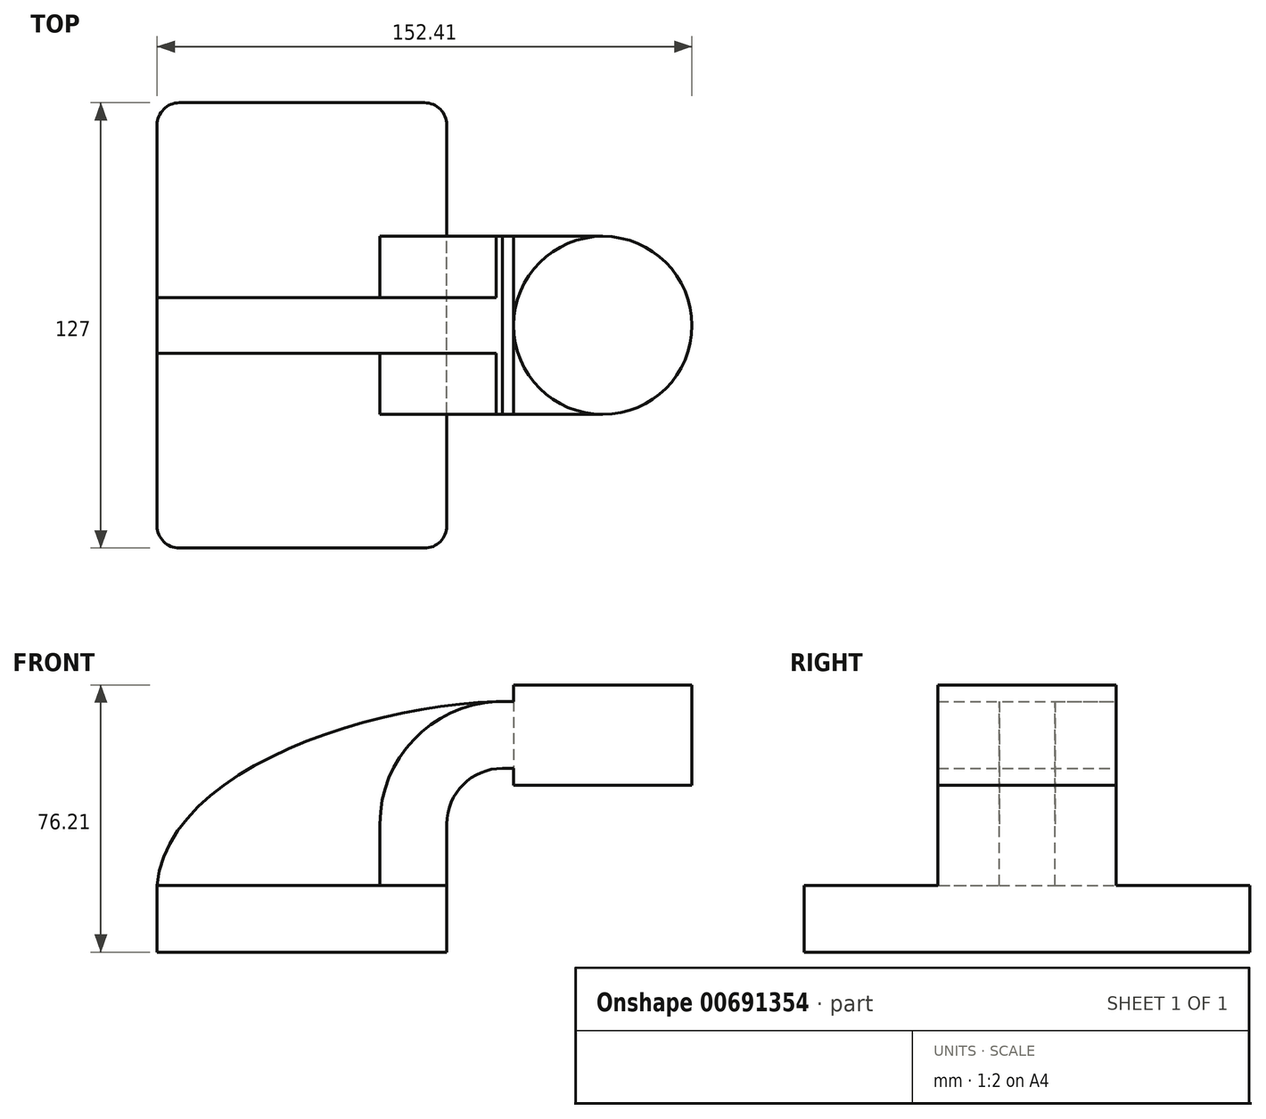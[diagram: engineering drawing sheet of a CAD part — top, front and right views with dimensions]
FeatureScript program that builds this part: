
annotation { "Feature Type Name" : "Feature", "Feature Type Description" : "" }
export const myFeature = defineFeature(function(context is Context, id is Id, definition is map)
    precondition{}
    {
        {
            var Q0;
            Q0=qCreatedBy(makeId("Front.planeOp"),FACE);
            var sketch = newSketch(context, id + "F0", { "sketchPlane" : qUnion([Q0])});
            skLineSegment(sketch, "E0.bottom", {"start": v(-41.28, 9.52) * mm, "end": v(41.27, 9.53) * mm});
            skLineSegment(sketch, "E0.top", {"start": v(-41.28, -9.52) * mm, "end": v(41.28, -9.52) * mm});
            skLineSegment(sketch, "E0.left", {"start": v(-41.28, 9.52) * mm, "end": v(-41.28, -9.53) * mm});
            skLineSegment(sketch, "E0.right", {"start": v(41.27, 9.53) * mm, "end": v(41.28, -9.52) * mm});
            skPoint(sketch, "E0.middle", {"position": v(0, 0) * mm});
            skLineSegment(sketch, "E1.bottom", {"start": v(60.32, 38.1) * mm, "end": v(111.12, 38.1) * mm});
            skLineSegment(sketch, "E1.top", {"start": v(60.32, 66.68) * mm, "end": v(111.12, 66.68) * mm});
            skLineSegment(sketch, "E1.left", {"start": v(60.32, 38.1) * mm, "end": v(60.32, 66.67) * mm});
            skLineSegment(sketch, "E1.right", {"start": v(111.12, 38.1) * mm, "end": v(111.12, 66.68) * mm});
            skPoint(sketch, "E1.middle", {"position": v(85.72, 52.39) * mm});
            skLineSegment(sketch, "E2", {"start": v(41.27, 9.53) * mm, "end": v(41.27, 27) * mm});
            skArc(sketch, "E3", {"start": v(41.27, 27) * mm, "mid": v(45.92, 38.23) * mm, "end": v(57.15, 42.88) * mm});
            skLineSegment(sketch, "E4", {"start": v(57.15, 42.88) * mm, "end": v(85.67, 42.88) * mm});
            skLineSegment(sketch, "E5.0", {"start": v(57.15, 61.93) * mm, "end": v(85.72, 61.93) * mm});
            skArc(sketch, "E5.1", {"start": v(22.22, 27) * mm, "mid": v(32.45, 51.7) * mm, "end": v(57.15, 61.93) * mm});
            skLineSegment(sketch, "E5.2", {"start": v(22.22, 9.53) * mm, "end": v(22.22, 27) * mm});
            skFitSpline(sketch, "E6", {"points": [v(-41.28, 9.52) * mm, v(57.15, 61.93) * mm], "startDerivative": vector(8.45, 98.1) * mm, "endDerivative": vector(115.67, 2.23) * mm});
            skLineSegment(sketch, "E7", {"start": v(85.72, 38.1) * mm, "end": v(85.72, 66.68) * mm});
            skSolve(sketch);
        }
        {
            var Q0;
            Q0=makeQuery(id+"F0.imprint","IMPRINT",FACE,{"disambiguationData":[TD([[makeQuery(id+"F0.imprint","IMPRINT",EDGE,{"derivedFrom":sQuery(id+"F0.wireOp",EDGE,"E0.top")}),1.0]])]});
            extrude(context, id + "F1", {"entities" : qUnion([Q0]), "endBound" : BoundingType.SYMMETRIC, "depth" : 127 * mm, "offsetDistance" : 25.4 * mm});
        }
        {
            var Q0;
            {var subQ1=sQuery(id+"F0.wireOp",EDGE,"E2");Q0=makeQuery(id+"F0.imprint","IMPRINT",FACE,{"disambiguationData":[TD([[makeQuery(id+"F0.imprint","IMPRINT",EDGE,{"derivedFrom":subQ1}),1.0]])]});}
            var Q1;
            {var subQ3=sQuery(id+"F0.wireOp",EDGE,"E1.left");var subQ5=sQuery(id+"F0.wireOp",EDGE,"E1.bottom");var subQ6=makeQuery(id+"F0.imprint","INTERSECT",VERTEX,{"derivedFrom":[subQ5,subQ3]});Q1=makeQuery(id+"F0.imprint","IMPRINT",FACE,{"disambiguationData":[TD([[makeQuery(id+"F0.imprint","IMPRINT",EDGE,{"disambiguationData":[TD([[subQ6,-1.0]])],"derivedFrom":subQ5}),1.0]])]});}
            var Q2;
            {var subQ0=sQuery(id+"F0.wireOp",EDGE,"E1.left");var subQ1=sQuery(id+"F0.wireOp",EDGE,"E1.top");var subQ2=makeQuery(id+"F0.imprint","INTERSECT",VERTEX,{"derivedFrom":[subQ1,subQ0]});Q2=makeQuery(id+"F0.imprint","IMPRINT",FACE,{"disambiguationData":[TD([[makeQuery(id+"F0.imprint","IMPRINT",EDGE,{"disambiguationData":[TD([[subQ2,-1.0]])],"derivedFrom":subQ1}),-1.0]])]});}
            extrude(context, id + "F2", {"entities" : qUnion([Q0, Q1, Q2]), "operationType" : NewBodyOperationType.ADD, "endBound" : BoundingType.SYMMETRIC, "depth" : 50.8 * mm, "offsetDistance" : 25.4 * mm});
        }
        {
            var Q0;
            {var subQ3=sQuery(id+"F0.wireOp",EDGE,"E5.2");Q0=makeQuery(id+"F0.imprint","IMPRINT",FACE,{"disambiguationData":[TD([[makeQuery(id+"F0.imprint","IMPRINT",EDGE,{"derivedFrom":subQ3}),1.0]])]});}
            extrude(context, id + "F3", {"entities" : qUnion([Q0]), "operationType" : NewBodyOperationType.ADD, "endBound" : BoundingType.SYMMETRIC, "depth" : 15.88 * mm, "offsetDistance" : 25.4 * mm});
        }
        {
            var Q0;
            {var subQ0=sQuery(id+"F0.wireOp",EDGE,"E1.right");Q0=makeQuery(id+"F0.imprint","IMPRINT",FACE,{"disambiguationData":[TD([[makeQuery(id+"F0.imprint","IMPRINT",EDGE,{"derivedFrom":subQ0}),1.0]])]});}
            var Q1;
            Q1 = qConstructionFilter(qBodyType(qCreatedBy(id + "FNUHMnEy8hkd5ea_0" ,EDGE), BodyType.WIRE), ConstructionObject.NO);
            var Q2;
            Q2=sQuery(id+"F0.wireOp",EDGE,"E7");
            revolve(context, id + "F4", {"entities" : qUnion([Q0]), "surfaceEntities" : qUnion([Q1]), "axis" : qUnion([Q2]), "revolveType" : RevolveType.FULL});
        }
        {
            var Q0;
            Q0=makeQuery(id+"F1.opExtrude","CAP_EDGE",EDGE,{"disambiguationData":[OSD([sQuery(id+"F0.wireOp",EDGE,"E0.right")])],"isStart":false});
            var Q1;
            Q1=makeQuery(id+"F1.opExtrude","CAP_EDGE",EDGE,{"disambiguationData":[OSD([sQuery(id+"F0.wireOp",EDGE,"E0.left")])],"isStart":false});
            var Q2;
            Q2=makeQuery(id+"F1.opExtrude","CAP_EDGE",EDGE,{"disambiguationData":[OSD([sQuery(id+"F0.wireOp",EDGE,"E0.left")])],"isStart":true});
            var Q3;
            Q3=makeQuery(id+"F1.opExtrude","CAP_EDGE",EDGE,{"disambiguationData":[OSD([sQuery(id+"F0.wireOp",EDGE,"E0.right")])],"isStart":true});
            fillet(context, id + "F5", {"entities" : qUnion([Q0, Q1, Q2, Q3]), "radius" : 6.35 * mm, "tangentPropagation" : true, "allowEdgeOverflow" : false});
        }
    });
